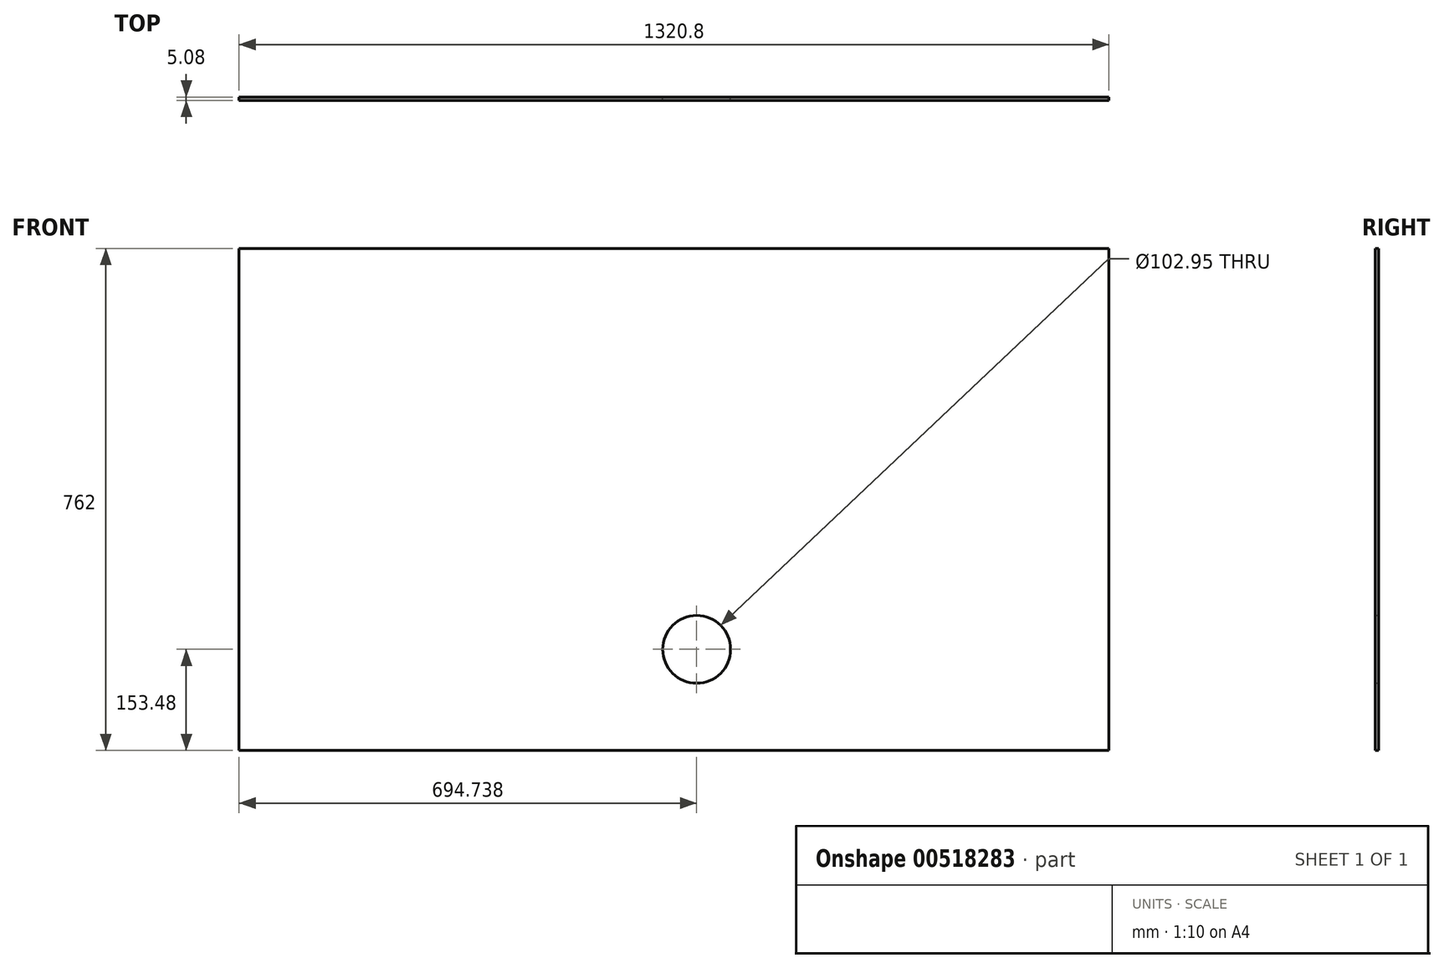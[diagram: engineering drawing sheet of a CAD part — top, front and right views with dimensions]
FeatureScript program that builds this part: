
annotation { "Feature Type Name" : "Feature", "Feature Type Description" : "" }
export const myFeature = defineFeature(function(context is Context, id is Id, definition is map)
    precondition{}
    {
        {
            var Q0;
            Q0=qCreatedBy(makeId("Front.planeOp"),FACE);
            var sketch = newSketch(context, id + "F0", { "sketchPlane" : qUnion([Q0])});
            skLineSegment(sketch, "E0.bottom", {"start": v(-681.83, -3.46) * mm, "end": v(638.97, -3.46) * mm});
            skLineSegment(sketch, "E0.top", {"start": v(-681.83, -765.46) * mm, "end": v(638.97, -765.46) * mm});
            skLineSegment(sketch, "E0.left", {"start": v(-681.83, -3.46) * mm, "end": v(-681.83, -765.46) * mm});
            skLineSegment(sketch, "E0.right", {"start": v(638.97, -3.46) * mm, "end": v(638.97, -765.46) * mm});
            skCircle(sketch, "E1", {"center": v(12.9, -611.98) * mm, "radius": 51.48 * mm});
            skSolve(sketch);
        }
        {
            var Q0;
            Q0=makeQuery(id+"F0.imprint","IMPRINT",FACE,{"disambiguationData":[TD([[makeQuery(id+"F0.imprint","IMPRINT",EDGE,{"derivedFrom":sQuery(id+"F0.wireOp",EDGE,"E0.bottom")}),-1.0]])]});
            extrude(context, id + "F1", {"entities" : qUnion([Q0]), "depth" : 5.08 * mm, "offsetDistance" : 25.4 * mm});
        }
    });
